# Revit family: 00044741_PORTALSSTUDIO_US2402H-US
name_source: partatom
category: Furniture Systems
units: mm (PartAtom-declared; Revit-internal decimal feet)

## family parameters
Always vertical = Yes
Cut with Voids When Loaded = No
Part Type = Normal
Room Calculation Point = No
Round Connector Dimension = Use Diameter
Shared = No
Work Plane-Based = No

## types (1)
- 00044741_PORTALSSTUDIO_US2402H-US
    Accessories = <By Category>
    Clad Roof = <By Category>
    Clad Side = <By Category>
    Description = Portal Studio
, 100"LX71"WX95"H
    Door Frame = <By Category>
    Door Glass = <By Category>
    Door Pull = <By Category>
    Fan = <By Category>
    Feet = <By Category>
    Inner Clad = <By Category>
    Lower Back Clad = <By Category>
    Lower Side Clad = <By Category>
    Manufacturer = Spacestor
    Model = US2402H
    Receptacle = <By Category>
    Rubber Frame = <By Category>
    Spot Light = <By Category>
    URL = https://spacestor.com
    Upper Back Clad = <By Category>
    Upper Side Clad = <By Category>
    Wire = <By Category>

## geometry (parser evidence)
native form markers: Sweep x2
no freeform markers — native parametric forms only
